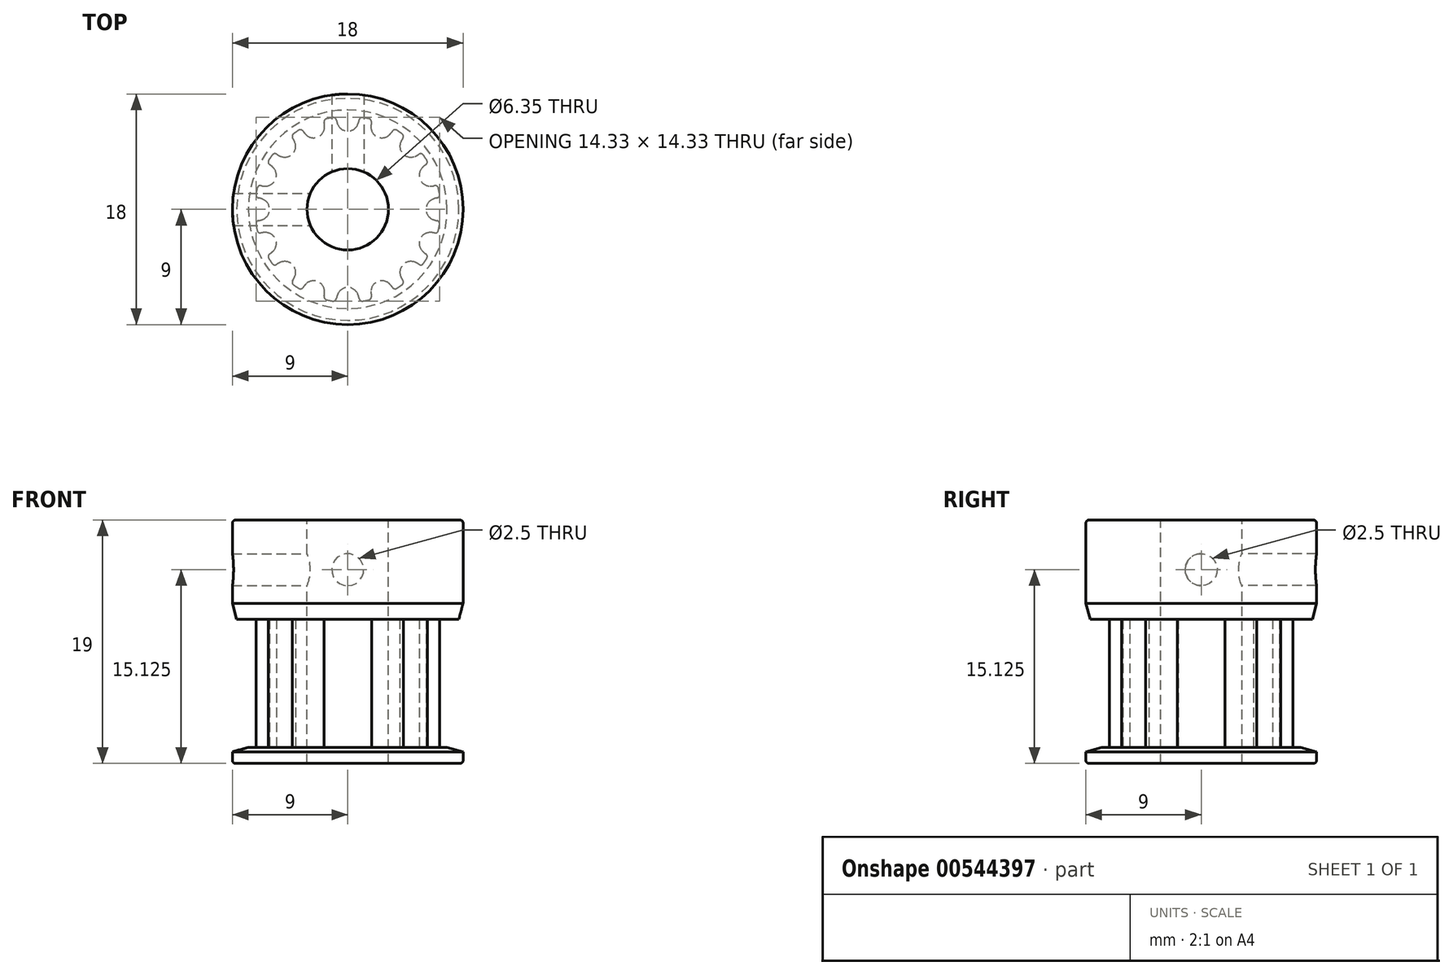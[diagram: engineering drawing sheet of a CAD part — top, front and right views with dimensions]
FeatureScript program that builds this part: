
annotation { "Feature Type Name" : "Feature", "Feature Type Description" : "" }
export const myFeature = defineFeature(function(context is Context, id is Id, definition is map)
    precondition{}
    {
        {
            assignVariable(context, id + "F0", {"name" : "teeth", "anyValue" : 16});
        }
        {
            assignVariable(context, id + "F1", {"name" : "width", "anyValue" : 10});
        }
        {
            var Q0;
            Q0=qCreatedBy(makeId("Top.planeOp"),FACE);
            var sketch = newSketch(context, id + "F2", { "sketchPlane" : qUnion([Q0])});
            skLineSegment(sketch, "E0", {"start": v(0, 0) * mm, "end": v(0, 6.1) * mm, "construction": true});
            skArc(sketch, "E1", {"start": v(1.86, 7.02) * mm, "mid": v(0, 7.26) * mm, "end": v(-1.86, 7.02) * mm, "construction": true});
            skArc(sketch, "E2", {"start": v(0, 6.1) * mm, "mid": v(0.46, 6.24) * mm, "end": v(0.77, 6.6) * mm});
            skLineSegment(sketch, "E3", {"start": v(0, 6.1) * mm, "end": v(0, 7.26) * mm, "construction": true});
            skLineSegment(sketch, "E4", {"start": v(0, 7.26) * mm, "end": v(0, 7.64) * mm, "construction": true});
            skArc(sketch, "E5", {"start": v(1.5, 7.5) * mm, "mid": v(0, 7.64) * mm, "end": v(-1.5, 7.5) * mm, "construction": true});
            skLineSegment(sketch, "E6", {"start": v(1.42, 7.12) * mm, "end": v(0, 0) * mm});
            skLineSegment(sketch, "E7", {"start": v(0, 0) * mm, "end": v(-1.42, 7.12) * mm});
            skArc(sketch, "E8", {"start": v(1.17, 7.16) * mm, "mid": v(0.99, 7.12) * mm, "end": v(0.89, 6.96) * mm});
            skArc(sketch, "E9", {"start": v(0.77, 6.6) * mm, "mid": v(0.84, 6.78) * mm, "end": v(0.89, 6.96) * mm});
            skArc(sketch, "E10.MirrorCS", {"start": v(0, 6.1) * mm, "mid": v(-0.46, 6.24) * mm, "end": v(-0.77, 6.6) * mm});
            skArc(sketch, "E11.MirrorCS", {"start": v(-0.77, 6.6) * mm, "mid": v(-0.84, 6.78) * mm, "end": v(-0.89, 6.96) * mm});
            skArc(sketch, "E12.MirrorCS", {"start": v(-1.17, 7.16) * mm, "mid": v(-0.99, 7.12) * mm, "end": v(-0.89, 6.96) * mm});
            skArc(sketch, "E13", {"start": v(0, 7.26) * mm, "mid": v(-0.3, 7.25) * mm, "end": v(-0.6, 7.23) * mm, "construction": true});
            skArc(sketch, "E14", {"start": v(1.65, 5.88) * mm, "mid": v(0, 6.1) * mm, "end": v(-1.65, 5.88) * mm, "construction": true});
            skArc(sketch, "E15", {"start": v(-1.17, 7.16) * mm, "mid": v(-1.3, 7.14) * mm, "end": v(-1.42, 7.12) * mm});
            skArc(sketch, "E16", {"start": v(1.17, 7.16) * mm, "mid": v(1.3, 7.14) * mm, "end": v(1.42, 7.12) * mm});
            skPoint(sketch, "E17", {"position": v(0, 6.1) * mm});
            skSolve(sketch);
        }
        {
            var Q0;
            Q0=makeQuery(id+"F2.imprint","IMPRINT",FACE,{"disambiguationData":[TD([[makeQuery(id+"F2.imprint","IMPRINT",EDGE,{"derivedFrom":sQuery(id+"F2.wireOp",EDGE,"E2")}),-1.0]])]});
            var Q1;
            {var subQ1=sQuery(id+"F2.wireOp",EDGE,"N9a9pOVT-NxnP-9PMo-Yz0L-ytRW1WlfzG62");Q1=makeQuery(id+"F2.imprint","IMPRINT",FACE,{"disambiguationData":[TD([[makeQuery(id+"F2.imprint","IMPRINT",EDGE,{"derivedFrom":subQ1}),-1.0]])]});}
            var Q2;
            {var subQ0=sQuery(id+"F2.wireOp",EDGE,"E6");Q2=makeQuery(id+"F2.imprint","IMPRINT",FACE,{"disambiguationData":[TD([[makeQuery(id+"F2.imprint","IMPRINT",EDGE,{"derivedFrom":subQ0}),-1.0]])]});}
            extrude(context, id + "F3", {"entities" : qUnion([Q0, Q1, Q2]), "depth" : (getVariable(context, 'width')) * mm, "offsetDistance" : 25 * mm, "symmetric" : true});
        }
        {
            var Q0;
            Q0=makeQuery(id+"F3.opExtrude","SWEPT_BODY",BODY,{"disambiguationData":[OSD([sQuery(id+"F2.wireOp",EDGE,"E1"),sQuery(id+"F2.wireOp",EDGE,"E2"),sQuery(id+"F2.wireOp",EDGE,"WtW3y5By-gfdo-wMA2-XeKf-OYMCoWhlFWBV"),sQuery(id+"F2.wireOp",EDGE,"E6"),sQuery(id+"F2.wireOp",EDGE,"E7"),sQuery(id+"F2.wireOp",EDGE,"N9a9pOVT-NxnP-9PMo-Yz0L-ytRW1WlfzG62"),sQuery(id+"F2.wireOp",EDGE,"E8"),sQuery(id+"F2.wireOp",EDGE,"E9"),sQuery(id+"F2.wireOp",EDGE,"E10.MirrorCS"),sQuery(id+"F2.wireOp",EDGE,"E11.MirrorCS"),sQuery(id+"F2.wireOp",EDGE,"E12.MirrorCS")])]});
            var Q1;
            Q1=makeQuery(id+"F3.opExtrude","SWEPT_EDGE",EDGE,{"disambiguationData":[OSD([sQuery(id+"F2.wireOp",EDGE,"E6"),sQuery(id+"F2.wireOp",EDGE,"E7")])]});
            circularPattern(context, id + "F4", {"operationType" : NewBodyOperationType.ADD, "entities" : qUnion([Q0]), "axis" : qUnion([Q1]), "angle" : 360 * degree, "instanceCount" : getVariable(context, 'teeth'), "equalSpace" : true});
        }
        {
            var Q0;
            {var subQ0=makeQuery(id+"F3.opExtrude","CAP_FACE",FACE,{"disambiguationData":[OSD([sQuery(id+"F2.wireOp",EDGE,"E2"),sQuery(id+"F2.wireOp",EDGE,"E6"),sQuery(id+"F2.wireOp",EDGE,"E7"),sQuery(id+"F2.wireOp",EDGE,"E8"),sQuery(id+"F2.wireOp",EDGE,"E9"),sQuery(id+"F2.wireOp",EDGE,"E10.MirrorCS"),sQuery(id+"F2.wireOp",EDGE,"E11.MirrorCS"),sQuery(id+"F2.wireOp",EDGE,"E12.MirrorCS"),sQuery(id+"F2.wireOp",EDGE,"E15"),sQuery(id+"F2.wireOp",EDGE,"E16")])],"isStart":true});Q0=makeQuery(id+"F4.boolean.opBoolean","MERGE",FACE,{"derivedFrom":[subQ0,makeQuery(id+"F4.opPattern","COPY",FACE,{"derivedFrom":subQ0,"instanceName":"1"}),makeQuery(id+"F4.opPattern","COPY",FACE,{"derivedFrom":subQ0,"instanceName":"2"}),makeQuery(id+"F4.opPattern","COPY",FACE,{"derivedFrom":subQ0,"instanceName":"3"}),makeQuery(id+"F4.opPattern","COPY",FACE,{"derivedFrom":subQ0,"instanceName":"4"}),makeQuery(id+"F4.opPattern","COPY",FACE,{"derivedFrom":subQ0,"instanceName":"5"}),makeQuery(id+"F4.opPattern","COPY",FACE,{"derivedFrom":subQ0,"instanceName":"6"}),makeQuery(id+"F4.opPattern","COPY",FACE,{"derivedFrom":subQ0,"instanceName":"7"}),makeQuery(id+"F4.opPattern","COPY",FACE,{"derivedFrom":subQ0,"instanceName":"8"}),makeQuery(id+"F4.opPattern","COPY",FACE,{"derivedFrom":subQ0,"instanceName":"9"}),makeQuery(id+"F4.opPattern","COPY",FACE,{"derivedFrom":subQ0,"instanceName":"10"}),makeQuery(id+"F4.opPattern","COPY",FACE,{"derivedFrom":subQ0,"instanceName":"11"}),makeQuery(id+"F4.opPattern","COPY",FACE,{"derivedFrom":subQ0,"instanceName":"12"}),makeQuery(id+"F4.opPattern","COPY",FACE,{"derivedFrom":subQ0,"instanceName":"13"}),makeQuery(id+"F4.opPattern","COPY",FACE,{"derivedFrom":subQ0,"instanceName":"14"}),makeQuery(id+"F4.opPattern","COPY",FACE,{"derivedFrom":subQ0,"instanceName":"15"}),makeQuery(id+"F4.opPattern","COPY",FACE,{"derivedFrom":subQ0,"instanceName":"16"}),makeQuery(id+"F4.opPattern","COPY",FACE,{"derivedFrom":subQ0,"instanceName":"17"}),makeQuery(id+"F4.opPattern","COPY",FACE,{"derivedFrom":subQ0,"instanceName":"18"}),makeQuery(id+"F4.opPattern","COPY",FACE,{"derivedFrom":subQ0,"instanceName":"19"}),makeQuery(id+"F4.opPattern","COPY",FACE,{"derivedFrom":subQ0,"instanceName":"20"}),makeQuery(id+"F4.opPattern","COPY",FACE,{"derivedFrom":subQ0,"instanceName":"21"}),makeQuery(id+"F4.opPattern","COPY",FACE,{"derivedFrom":subQ0,"instanceName":"22"}),makeQuery(id+"F4.opPattern","COPY",FACE,{"derivedFrom":subQ0,"instanceName":"23"}),makeQuery(id+"F4.opPattern","COPY",FACE,{"derivedFrom":subQ0,"instanceName":"24"}),makeQuery(id+"F4.opPattern","COPY",FACE,{"derivedFrom":subQ0,"instanceName":"25"}),makeQuery(id+"F4.opPattern","COPY",FACE,{"derivedFrom":subQ0,"instanceName":"26"}),makeQuery(id+"F4.opPattern","COPY",FACE,{"derivedFrom":subQ0,"instanceName":"27"}),makeQuery(id+"F4.opPattern","COPY",FACE,{"derivedFrom":subQ0,"instanceName":"28"}),makeQuery(id+"F4.opPattern","COPY",FACE,{"derivedFrom":subQ0,"instanceName":"29"}),makeQuery(id+"F4.opPattern","COPY",FACE,{"derivedFrom":subQ0,"instanceName":"30"}),makeQuery(id+"F4.opPattern","COPY",FACE,{"derivedFrom":subQ0,"instanceName":"31"}),makeQuery(id+"F4.opPattern","COPY",FACE,{"derivedFrom":subQ0,"instanceName":"32"}),makeQuery(id+"F4.opPattern","COPY",FACE,{"derivedFrom":subQ0,"instanceName":"33"}),makeQuery(id+"F4.opPattern","COPY",FACE,{"derivedFrom":subQ0,"instanceName":"34"}),makeQuery(id+"F4.opPattern","COPY",FACE,{"derivedFrom":subQ0,"instanceName":"35"}),makeQuery(id+"F4.opPattern","COPY",FACE,{"derivedFrom":subQ0,"instanceName":"36"}),makeQuery(id+"F4.opPattern","COPY",FACE,{"derivedFrom":subQ0,"instanceName":"37"}),makeQuery(id+"F4.opPattern","COPY",FACE,{"derivedFrom":subQ0,"instanceName":"38"}),makeQuery(id+"F4.opPattern","COPY",FACE,{"derivedFrom":subQ0,"instanceName":"39"})]});}
            var sketch = newSketch(context, id + "F5", { "sketchPlane" : qUnion([Q0])});
            skCircle(sketch, "E18", {"center": v(0, 0) * mm, "radius": 9 * mm});
            skSolve(sketch);
        }
        {
            var Q0;
            Q0=qSketchRegion(id+"F5",true);
            extrude(context, id + "F6", {"entities" : qUnion([Q0]), "operationType" : NewBodyOperationType.ADD, "depth" : 1.25 * mm, "offsetDistance" : 25 * mm});
        }
        {
            var Q0;
            {var subQ0=makeQuery(id+"F3.opExtrude","CAP_FACE",FACE,{"disambiguationData":[OSD([sQuery(id+"F2.wireOp",EDGE,"E2"),sQuery(id+"F2.wireOp",EDGE,"E6"),sQuery(id+"F2.wireOp",EDGE,"E7"),sQuery(id+"F2.wireOp",EDGE,"E8"),sQuery(id+"F2.wireOp",EDGE,"E9"),sQuery(id+"F2.wireOp",EDGE,"E10.MirrorCS"),sQuery(id+"F2.wireOp",EDGE,"E11.MirrorCS"),sQuery(id+"F2.wireOp",EDGE,"E12.MirrorCS"),sQuery(id+"F2.wireOp",EDGE,"E15"),sQuery(id+"F2.wireOp",EDGE,"E16")])],"isStart":false});Q0=makeQuery(id+"F4.boolean.opBoolean","MERGE",FACE,{"derivedFrom":[subQ0,makeQuery(id+"F4.opPattern","COPY",FACE,{"derivedFrom":subQ0,"instanceName":"1"}),makeQuery(id+"F4.opPattern","COPY",FACE,{"derivedFrom":subQ0,"instanceName":"2"}),makeQuery(id+"F4.opPattern","COPY",FACE,{"derivedFrom":subQ0,"instanceName":"3"}),makeQuery(id+"F4.opPattern","COPY",FACE,{"derivedFrom":subQ0,"instanceName":"4"}),makeQuery(id+"F4.opPattern","COPY",FACE,{"derivedFrom":subQ0,"instanceName":"5"}),makeQuery(id+"F4.opPattern","COPY",FACE,{"derivedFrom":subQ0,"instanceName":"6"}),makeQuery(id+"F4.opPattern","COPY",FACE,{"derivedFrom":subQ0,"instanceName":"7"}),makeQuery(id+"F4.opPattern","COPY",FACE,{"derivedFrom":subQ0,"instanceName":"8"}),makeQuery(id+"F4.opPattern","COPY",FACE,{"derivedFrom":subQ0,"instanceName":"9"}),makeQuery(id+"F4.opPattern","COPY",FACE,{"derivedFrom":subQ0,"instanceName":"10"}),makeQuery(id+"F4.opPattern","COPY",FACE,{"derivedFrom":subQ0,"instanceName":"11"}),makeQuery(id+"F4.opPattern","COPY",FACE,{"derivedFrom":subQ0,"instanceName":"12"}),makeQuery(id+"F4.opPattern","COPY",FACE,{"derivedFrom":subQ0,"instanceName":"13"}),makeQuery(id+"F4.opPattern","COPY",FACE,{"derivedFrom":subQ0,"instanceName":"14"}),makeQuery(id+"F4.opPattern","COPY",FACE,{"derivedFrom":subQ0,"instanceName":"15"}),makeQuery(id+"F4.opPattern","COPY",FACE,{"derivedFrom":subQ0,"instanceName":"16"}),makeQuery(id+"F4.opPattern","COPY",FACE,{"derivedFrom":subQ0,"instanceName":"17"}),makeQuery(id+"F4.opPattern","COPY",FACE,{"derivedFrom":subQ0,"instanceName":"18"}),makeQuery(id+"F4.opPattern","COPY",FACE,{"derivedFrom":subQ0,"instanceName":"19"}),makeQuery(id+"F4.opPattern","COPY",FACE,{"derivedFrom":subQ0,"instanceName":"20"}),makeQuery(id+"F4.opPattern","COPY",FACE,{"derivedFrom":subQ0,"instanceName":"21"}),makeQuery(id+"F4.opPattern","COPY",FACE,{"derivedFrom":subQ0,"instanceName":"22"}),makeQuery(id+"F4.opPattern","COPY",FACE,{"derivedFrom":subQ0,"instanceName":"23"}),makeQuery(id+"F4.opPattern","COPY",FACE,{"derivedFrom":subQ0,"instanceName":"24"}),makeQuery(id+"F4.opPattern","COPY",FACE,{"derivedFrom":subQ0,"instanceName":"25"}),makeQuery(id+"F4.opPattern","COPY",FACE,{"derivedFrom":subQ0,"instanceName":"26"}),makeQuery(id+"F4.opPattern","COPY",FACE,{"derivedFrom":subQ0,"instanceName":"27"}),makeQuery(id+"F4.opPattern","COPY",FACE,{"derivedFrom":subQ0,"instanceName":"28"}),makeQuery(id+"F4.opPattern","COPY",FACE,{"derivedFrom":subQ0,"instanceName":"29"}),makeQuery(id+"F4.opPattern","COPY",FACE,{"derivedFrom":subQ0,"instanceName":"30"}),makeQuery(id+"F4.opPattern","COPY",FACE,{"derivedFrom":subQ0,"instanceName":"31"}),makeQuery(id+"F4.opPattern","COPY",FACE,{"derivedFrom":subQ0,"instanceName":"32"}),makeQuery(id+"F4.opPattern","COPY",FACE,{"derivedFrom":subQ0,"instanceName":"33"}),makeQuery(id+"F4.opPattern","COPY",FACE,{"derivedFrom":subQ0,"instanceName":"34"}),makeQuery(id+"F4.opPattern","COPY",FACE,{"derivedFrom":subQ0,"instanceName":"35"}),makeQuery(id+"F4.opPattern","COPY",FACE,{"derivedFrom":subQ0,"instanceName":"36"}),makeQuery(id+"F4.opPattern","COPY",FACE,{"derivedFrom":subQ0,"instanceName":"37"}),makeQuery(id+"F4.opPattern","COPY",FACE,{"derivedFrom":subQ0,"instanceName":"38"}),makeQuery(id+"F4.opPattern","COPY",FACE,{"derivedFrom":subQ0,"instanceName":"39"})]});}
            var sketch = newSketch(context, id + "F7", { "sketchPlane" : qUnion([Q0])});
            skCircle(sketch, "E19", {"center": v(0, 0) * mm, "radius": 9 * mm});
            skSolve(sketch);
        }
        {
            var Q0;
            Q0=qSketchRegion(id+"F7",true);
            extrude(context, id + "F8", {"entities" : qUnion([Q0]), "operationType" : NewBodyOperationType.ADD, "depth" : 1.25 * mm, "offsetDistance" : 25 * mm});
        }
        {
            var Q0;
            Q0=makeQuery(id+"F8.opExtrude","CAP_FACE",FACE,{"disambiguationData":[OSD([sQuery(id+"F7.wireOp",EDGE,"E19")])],"isStart":false});
            var sketch = newSketch(context, id + "F9", { "sketchPlane" : qUnion([Q0])});
            skCircle(sketch, "E20", {"center": v(0, 0) * mm, "radius": 9 * mm});
            skSolve(sketch);
        }
        {
            var Q0;
            Q0=qSketchRegion(id+"F9",true);
            extrude(context, id + "F10", {"entities" : qUnion([Q0]), "operationType" : NewBodyOperationType.ADD, "depth" : (19 - 10 - 2 * 1.25) * mm, "offsetDistance" : 25 * mm});
        }
        {
            var Q0;
            Q0=makeQuery(id+"F10.opExtrude","CAP_FACE",FACE,{"disambiguationData":[OSD([sQuery(id+"F9.wireOp",EDGE,"E20")])],"isStart":false});
            var sketch = newSketch(context, id + "F11", { "sketchPlane" : qUnion([Q0])});
            skCircle(sketch, "E21", {"center": v(0, 0) * mm, "radius": 3.18 * mm});
            skSolve(sketch);
        }
        {
            var Q0;
            Q0=qSketchRegion(id+"F11",true);
            extrude(context, id + "F12", {"entities" : qUnion([Q0]), "operationType" : NewBodyOperationType.REMOVE, "endBound" : BoundingType.THROUGH_ALL, "oppositeDirection" : true, "depth" : 25 * mm, "offsetDistance" : 25 * mm});
        }
        {
            var Q0;
            Q0=qCreatedBy(makeId("Front.planeOp"),FACE);
            var sketch = newSketch(context, id + "F13", { "sketchPlane" : qUnion([Q0])});
            skCircle(sketch, "E22", {"center": v(0, 8.88) * mm, "radius": 1.25 * mm});
            skLineSegment(sketch, "E23", {"start": v(12.52, 12.75) * mm, "end": v(-11.32, 12.75) * mm, "construction": true});
            skLineSegment(sketch, "E24", {"start": v(11.95, 8.88) * mm, "end": v(-11.1, 8.88) * mm, "construction": true});
            skLineSegment(sketch, "E25", {"start": v(12.33, 5) * mm, "end": v(-11.51, 5) * mm, "construction": true});
            skSolve(sketch);
        }
        {
            var Q0;
            Q0=qSketchRegion(id+"F13",true);
            extrude(context, id + "F14", {"entities" : qUnion([Q0]), "operationType" : NewBodyOperationType.REMOVE, "endBound" : BoundingType.THROUGH_ALL, "oppositeDirection" : true, "depth" : 25 * mm, "offsetDistance" : 25 * mm});
        }
        {
            var Q0;
            Q0=qCreatedBy(makeId("Right.planeOp"),FACE);
            var sketch = newSketch(context, id + "F15", { "sketchPlane" : qUnion([Q0])});
            skCircle(sketch, "E26", {"center": v(0, 8.88) * mm, "radius": 1.25 * mm});
            skSolve(sketch);
        }
        {
            var Q0;
            Q0=qSketchRegion(id+"F15",true);
            extrude(context, id + "F16", {"entities" : qUnion([Q0]), "operationType" : NewBodyOperationType.REMOVE, "endBound" : BoundingType.THROUGH_ALL, "oppositeDirection" : true, "depth" : 25 * mm, "offsetDistance" : 25 * mm});
        }
        {
            var Q0;
            Q0=makeQuery(id+"F6.opExtrude","CAP_EDGE",EDGE,{"disambiguationData":[OSD([sQuery(id+"F5.wireOp",EDGE,"E18")])],"isStart":true});
            var Q1;
            Q1=makeQuery(id+"F8.opExtrude","CAP_EDGE",EDGE,{"disambiguationData":[OSD([sQuery(id+"F7.wireOp",EDGE,"E19")])],"isStart":true});
            chamfer(context, id + "F17", {"entities" : qUnion([Q0, Q1]), "chamferType" : ChamferType.OFFSET_ANGLE, "width" : 1.25 * mm, "oppositeDirection" : true, "angle" : 15 * degree, "tangentPropagation" : true});
        }
        {
            var Q0;
            Q0=makeQuery(id+"F10.opExtrude","CAP_EDGE",EDGE,{"disambiguationData":[OSD([sQuery(id+"F9.wireOp",EDGE,"E20")])],"isStart":true});
            var Q1;
            Q1=makeQuery(id+"F10.opExtrude","CAP_EDGE",EDGE,{"disambiguationData":[OSD([sQuery(id+"F9.wireOp",EDGE,"E20")])],"isStart":false});
            var Q2;
            Q2=makeQuery(id+"F8.opExtrude","CAP_EDGE",EDGE,{"disambiguationData":[OSD([sQuery(id+"F7.wireOp",EDGE,"E19")])],"isStart":false});
            var Q3;
            Q3=makeQuery(id+"F6.opExtrude","CAP_EDGE",EDGE,{"disambiguationData":[OSD([sQuery(id+"F5.wireOp",EDGE,"E18")])],"isStart":false});
            fillet(context, id + "F18", {"entities" : qUnion([Q0, Q1, Q2, Q3]), "radius" : 0.25 * mm, "tangentPropagation" : true, "allowEdgeOverflow" : false});
        }
    });
